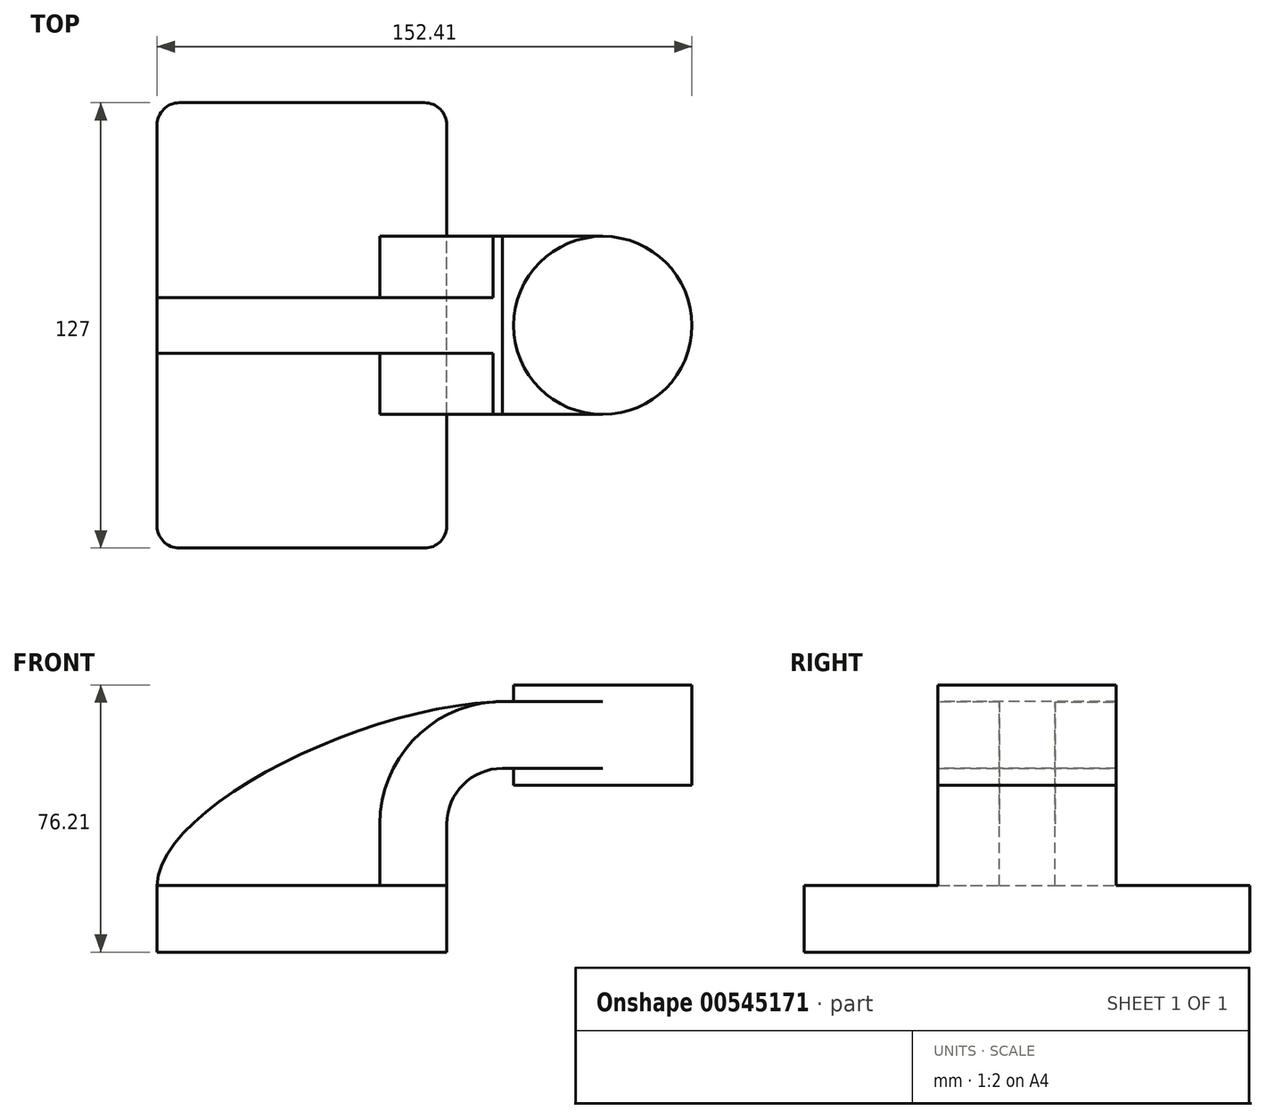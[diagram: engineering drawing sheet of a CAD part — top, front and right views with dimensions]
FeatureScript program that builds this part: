
annotation { "Feature Type Name" : "Feature", "Feature Type Description" : "" }
export const myFeature = defineFeature(function(context is Context, id is Id, definition is map)
    precondition{}
    {
        {
            var Q0;
            Q0=qCreatedBy(makeId("Front.planeOp"),FACE);
            var sketch = newSketch(context, id + "F0", { "sketchPlane" : qUnion([Q0])});
            skLineSegment(sketch, "E0.bottom", {"start": v(-41.28, 9.52) * mm, "end": v(41.28, 9.53) * mm});
            skLineSegment(sketch, "E0.top", {"start": v(-41.28, -9.53) * mm, "end": v(41.28, -9.53) * mm});
            skLineSegment(sketch, "E0.left", {"start": v(-41.28, 9.52) * mm, "end": v(-41.28, -9.53) * mm});
            skLineSegment(sketch, "E0.right", {"start": v(41.28, 9.53) * mm, "end": v(41.28, -9.52) * mm});
            skPoint(sketch, "E0.middle", {"position": v(0, 0) * mm});
            skLineSegment(sketch, "E1.bottom", {"start": v(111.12, 38.1) * mm, "end": v(60.32, 38.1) * mm});
            skLineSegment(sketch, "E1.top", {"start": v(111.12, 66.68) * mm, "end": v(60.32, 66.68) * mm});
            skLineSegment(sketch, "E1.left", {"start": v(111.12, 38.1) * mm, "end": v(111.12, 66.68) * mm});
            skLineSegment(sketch, "E1.right", {"start": v(60.32, 38.1) * mm, "end": v(60.32, 66.67) * mm});
            skPoint(sketch, "E1.middle", {"position": v(85.72, 52.39) * mm});
            skLineSegment(sketch, "E2", {"start": v(41.27, 9.53) * mm, "end": v(41.27, 27) * mm});
            skArc(sketch, "E3", {"start": v(41.27, 27) * mm, "mid": v(45.92, 38.23) * mm, "end": v(57.15, 42.88) * mm});
            skLineSegment(sketch, "E4", {"start": v(57.15, 42.88) * mm, "end": v(85.72, 42.88) * mm});
            skPoint(sketch, "E4.endSnap0", {"position": v(85.72, 38.1) * mm});
            skLineSegment(sketch, "E5.0", {"start": v(57.15, 61.93) * mm, "end": v(85.72, 61.93) * mm});
            skArc(sketch, "E5.1", {"start": v(22.22, 27) * mm, "mid": v(32.45, 51.7) * mm, "end": v(57.15, 61.93) * mm});
            skLineSegment(sketch, "E5.2", {"start": v(22.22, 9.53) * mm, "end": v(22.22, 27) * mm});
            skLineSegment(sketch, "E6", {"start": v(85.72, 52.39) * mm, "end": v(85.72, 66.68) * mm});
            skFitSpline(sketch, "E7", {"points": [v(-41.28, 9.52) * mm, v(57.15, 61.93) * mm], "startDerivative": vector(1.9, 67.6) * mm, "endDerivative": vector(118, 2.79) * mm});
            skLineSegment(sketch, "E8", {"start": v(85.72, 52.39) * mm, "end": v(85.72, 38.1) * mm});
            skSolve(sketch);
        }
        {
            var Q0;
            Q0=makeQuery(id+"F0.imprint","IMPRINT",FACE,{"disambiguationData":[TD([[makeQuery(id+"F0.imprint","IMPRINT",EDGE,{"derivedFrom":sQuery(id+"F0.wireOp",EDGE,"E0.top")}),1.0]])]});
            extrude(context, id + "F1", {"entities" : qUnion([Q0]), "endBound" : BoundingType.SYMMETRIC, "depth" : 127 * mm, "offsetDistance" : 25.4 * mm});
        }
        {
            var Q0;
            {var subQ1=sQuery(id+"F0.wireOp",EDGE,"E2");Q0=makeQuery(id+"F0.imprint","IMPRINT",FACE,{"disambiguationData":[TD([[makeQuery(id+"F0.imprint","IMPRINT",EDGE,{"derivedFrom":subQ1}),1.0]])]});}
            var Q1;
            {var subQ5=sQuery(id+"F0.wireOp",EDGE,"E4");var subQ6=sQuery(id+"F0.wireOp",EDGE,"E1.right");var subQ7=makeQuery(id+"F0.imprint","INTERSECT",VERTEX,{"derivedFrom":[subQ6,subQ5]});Q1=makeQuery(id+"F0.imprint","IMPRINT",FACE,{"disambiguationData":[TD([[makeQuery(id+"F0.imprint","IMPRINT",EDGE,{"disambiguationData":[TD([[subQ7,-1.0]])],"derivedFrom":subQ6}),-1.0]])]});}
            extrude(context, id + "F2", {"entities" : qUnion([Q0, Q1]), "operationType" : NewBodyOperationType.ADD, "endBound" : BoundingType.SYMMETRIC, "depth" : 50.8 * mm, "offsetDistance" : 25.4 * mm});
        }
        {
            var Q0;
            {var subQ3=sQuery(id+"F0.wireOp",EDGE,"E5.2");Q0=makeQuery(id+"F0.imprint","IMPRINT",FACE,{"disambiguationData":[TD([[makeQuery(id+"F0.imprint","IMPRINT",EDGE,{"derivedFrom":subQ3}),1.0]])]});}
            extrude(context, id + "F3", {"entities" : qUnion([Q0]), "operationType" : NewBodyOperationType.ADD, "endBound" : BoundingType.SYMMETRIC, "depth" : 15.88 * mm, "offsetDistance" : 25.4 * mm});
        }
        {
            var Q0;
            {var subQ0=sQuery(id+"F0.wireOp",EDGE,"E1.left");Q0=makeQuery(id+"F0.imprint","IMPRINT",FACE,{"disambiguationData":[TD([[makeQuery(id+"F0.imprint","IMPRINT",EDGE,{"derivedFrom":subQ0}),1.0]])]});}
            var Q1;
            Q1=sQuery(id+"F0.wireOp",EDGE,"E8");
            revolve(context, id + "F4", {"operationType" : NewBodyOperationType.ADD, "entities" : qUnion([Q0]), "axis" : qUnion([Q1]), "revolveType" : RevolveType.FULL});
        }
        {
            var Q0;
            Q0=makeQuery(id+"F1.opExtrude","CAP_EDGE",EDGE,{"disambiguationData":[OSD([sQuery(id+"F0.wireOp",EDGE,"E0.left")])],"isStart":false});
            var Q1;
            Q1=makeQuery(id+"F1.opExtrude","CAP_EDGE",EDGE,{"disambiguationData":[OSD([sQuery(id+"F0.wireOp",EDGE,"E0.right")])],"isStart":false});
            var Q2;
            Q2=makeQuery(id+"F1.opExtrude","CAP_EDGE",EDGE,{"disambiguationData":[OSD([sQuery(id+"F0.wireOp",EDGE,"E0.right")])],"isStart":true});
            var Q3;
            Q3=makeQuery(id+"F1.opExtrude","CAP_EDGE",EDGE,{"disambiguationData":[OSD([sQuery(id+"F0.wireOp",EDGE,"E0.left")])],"isStart":true});
            fillet(context, id + "F5", {"entities" : qUnion([Q0, Q1, Q2, Q3]), "radius" : 6.35 * mm, "tangentPropagation" : true, "allowEdgeOverflow" : false});
        }
    });
